# Revit family: WVA-6
name_source: partatom
category: Mechanical Equipment
revit_build: Autodesk Revit MEP 2014 (Build: 20140709_2115(x64)
units: mm (PartAtom-declared; Revit-internal decimal feet)

## types (1)
- WVA-6
    A = 19"
    ApproximateShipmentWeight = 375 lbs
    ArrayRadius = 8 3/8"
    B = 39"
    BottomExtrusionHeight = 3/8"
    BottomRevolveHeight = 4 1/4"
    C = 27 3/4"
    CouplingHeight = 6"
    CylindarDia = 13 1/4"
    CylinderHalfLength = 9 1/2"
    CylinderHeight = 30 1/2"
    D = 19 1/2"
    Height1 = 1 1/4"
    Height2 = 1/4"
    HookDiameter = 3/8"
    HookDistance = 3 3/4"
    HookTopDistance = 1/2"
    HookWidth = 3/4"
    LeftHookDistance = 3/8"
    Manufacturer = Wessels Company
    MaximumFlow = 570 GPM
    MaximumOperatingPressure = 125 PSIG
    MaximumOperatingTemperature = 240°F
    Model = WVA-6
    NumberOfArray = 9
    PartNumber = 72080060
    PipeConnectorDiameter = 6"
    PipeDiameter = 6 5/8"
    RevolveRadius = 6 5/8"
    RingDistance = 7 5/8"
    SideDrainExtrusion = 1 1/4"
    SideFlangeStep1 = 7 1/2"
    SideFlangeStep2 = 11"
    SideFlangeThickness = 1"
    SideFlangeThickness1 = 1/2"
    Step1Diameter = 1"
    Step2Diameter = 2 1/8"
    Step3Diameter = 3 1/2"
    Step4Diameter = 4 7/8"
    Step5Diameter = 4 1/8"
    TopExtrusionDiameter = 2 1/8"
    TotalHeight = 5 3/8"
    URL = http://westank.com

## geometry (parser evidence)
native form markers: Extrusion x3, Revolve x1, Sweep x5
no freeform markers — native parametric forms only
